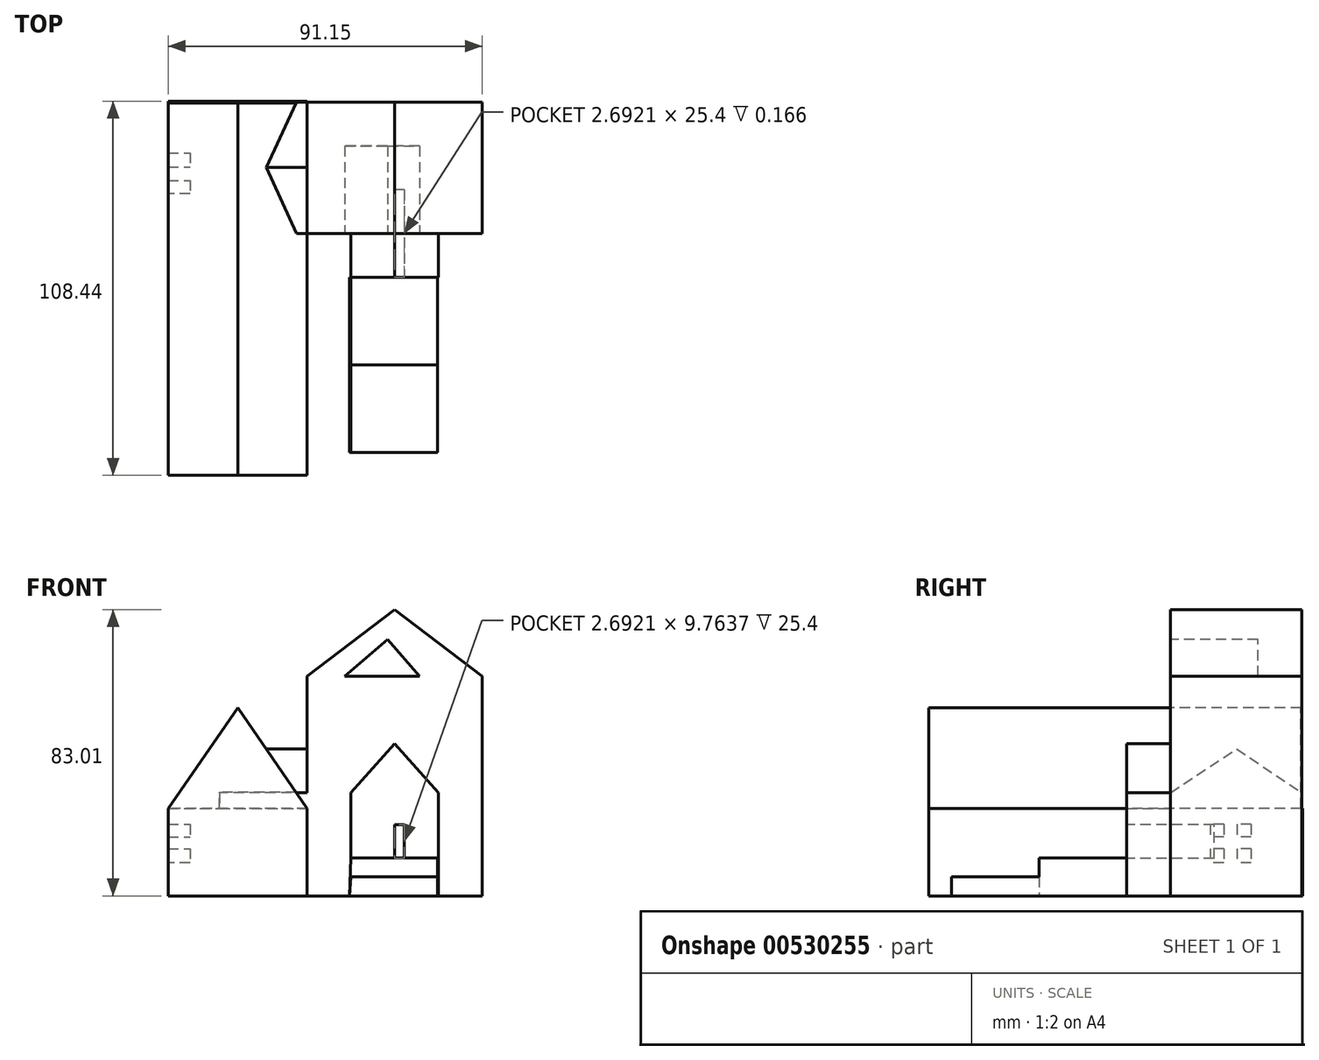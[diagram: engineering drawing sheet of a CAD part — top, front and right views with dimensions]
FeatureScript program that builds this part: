
annotation { "Feature Type Name" : "Feature", "Feature Type Description" : "" }
export const myFeature = defineFeature(function(context is Context, id is Id, definition is map)
    precondition{}
    {
        {
            var Q0;
            Q0=qCreatedBy(makeId("Right.planeOp"),FACE);
            var sketch = newSketch(context, id + "F0", { "sketchPlane" : qUnion([Q0])});
            skLineSegment(sketch, "E0.bottom", {"start": v(61.84, 29.91) * mm, "end": v(23.74, 29.91) * mm});
            skLineSegment(sketch, "E0.top", {"start": v(61.84, 10.86) * mm, "end": v(23.74, 10.86) * mm});
            skLineSegment(sketch, "E0.left", {"start": v(61.84, 29.91) * mm, "end": v(61.84, 10.86) * mm});
            skLineSegment(sketch, "E0.right", {"start": v(23.74, 29.91) * mm, "end": v(23.74, 10.86) * mm});
            skLineSegment(sketch, "E1", {"start": v(61.84, 29.91) * mm, "end": v(42.98, 42.61) * mm});
            skLineSegment(sketch, "E2", {"start": v(42.98, 42.61) * mm, "end": v(23.74, 29.91) * mm});
            skLineSegment(sketch, "E3", {"start": v(23.74, 29.91) * mm, "end": v(23.74, 42.61) * mm});
            skLineSegment(sketch, "E4", {"start": v(23.74, 42.61) * mm, "end": v(61.84, 42.61) * mm});
            skLineSegment(sketch, "E5", {"start": v(61.84, 42.61) * mm, "end": v(61.84, 29.91) * mm});
            skSolve(sketch);
        }
        {
            var Q0;
            Q0=makeQuery(id+"F0.imprint","IMPRINT",FACE,{"disambiguationData":[TD([[makeQuery(id+"F0.imprint","IMPRINT",EDGE,{"derivedFrom":sQuery(id+"F0.wireOp",EDGE,"E0.bottom")}),1.0]])]});
            var Q1;
            Q1=makeQuery(id+"F0.imprint","IMPRINT",FACE,{"disambiguationData":[TD([[makeQuery(id+"F0.imprint","IMPRINT",EDGE,{"derivedFrom":sQuery(id+"F0.wireOp",EDGE,"E0.bottom")}),-1.0]])]});
            extrude(context, id + "F1", {"entities" : qUnion([Q0, Q1]), "depth" : 50.8 * mm, "offsetDistance" : 25.4 * mm});
        }
        {
            var Q0;
            Q0=makeQuery(id+"F1.opExtrude","SWEPT_FACE",FACE,{"disambiguationData":[OSD([sQuery(id+"F0.wireOp",EDGE,"E0.right")])]});
            var sketch = newSketch(context, id + "F2", { "sketchPlane" : qUnion([Q0])});
            skLineSegment(sketch, "E6", {"start": v(12.7, 10.86) * mm, "end": v(12.7, 29.91) * mm});
            skLineSegment(sketch, "E7", {"start": v(12.7, 29.91) * mm, "end": v(38.1, 29.91) * mm});
            skLineSegment(sketch, "E8", {"start": v(38.1, 29.91) * mm, "end": v(38.1, 10.86) * mm});
            skLineSegment(sketch, "E9", {"start": v(38.1, 10.86) * mm, "end": v(12.7, 10.86) * mm});
            skSolve(sketch);
        }
        {
            var Q0;
            Q0 = qSketchRegion(id + "F2", true);
            extrude(context, id + "F3", {"entities" : qUnion([Q0]), "operationType" : NewBodyOperationType.ADD, "depth" : 12.7 * mm, "offsetDistance" : 25.4 * mm});
        }
        {
            var Q0;
            Q0=makeQuery(id+"F3.opExtrude","CAP_FACE",FACE,{"disambiguationData":[OSD([sQuery(id+"F2.wireOp",EDGE,"E6"),sQuery(id+"F2.wireOp",EDGE,"E7"),sQuery(id+"F2.wireOp",EDGE,"E8"),sQuery(id+"F2.wireOp",EDGE,"E9")])],"isStart":false});
            var sketch = newSketch(context, id + "F4", { "sketchPlane" : qUnion([Q0])});
            skLineSegment(sketch, "E10", {"start": v(12.7, 29.91) * mm, "end": v(25.4, 44.11) * mm});
            skLineSegment(sketch, "E11", {"start": v(25.4, 44.11) * mm, "end": v(38.1, 29.91) * mm});
            skLineSegment(sketch, "E12", {"start": v(38.1, 29.91) * mm, "end": v(12.7, 29.91) * mm});
            skSolve(sketch);
        }
        {
            var Q0;
            Q0 = qSketchRegion(id + "F4", true);
            extrude(context, id + "F5", {"entities" : qUnion([Q0]), "operationType" : NewBodyOperationType.ADD, "oppositeDirection" : true, "depth" : 31.75 * mm, "offsetDistance" : 25.4 * mm});
        }
        {
            var Q0;
            Q0=makeQuery(id+"F5.boolean.opBoolean","MERGE",FACE,{"derivedFrom":[makeQuery(id+"F3.opExtrude","CAP_FACE",FACE,{"disambiguationData":[OSD([sQuery(id+"F2.wireOp",EDGE,"E6"),sQuery(id+"F2.wireOp",EDGE,"E7"),sQuery(id+"F2.wireOp",EDGE,"E8"),sQuery(id+"F2.wireOp",EDGE,"E9")])],"isStart":false}),makeQuery(id+"F5.opExtrude","CAP_FACE",FACE,{"disambiguationData":[OSD([sQuery(id+"F4.wireOp",EDGE,"E10"),sQuery(id+"F4.wireOp",EDGE,"E11"),sQuery(id+"F4.wireOp",EDGE,"E12")])],"isStart":true})]});
            var sketch = newSketch(context, id + "F6", { "sketchPlane" : qUnion([Q0])});
            skLineSegment(sketch, "E13.bottom", {"start": v(25.4, 10.86) * mm, "end": v(28.1, 10.86) * mm});
            skLineSegment(sketch, "E13.top", {"start": v(25.4, 20.63) * mm, "end": v(28.1, 20.63) * mm});
            skLineSegment(sketch, "E13.left", {"start": v(25.4, 10.86) * mm, "end": v(25.4, 20.63) * mm});
            skLineSegment(sketch, "E13.right", {"start": v(28.1, 10.86) * mm, "end": v(28.1, 20.63) * mm});
            skSolve(sketch);
        }
        {
            var Q0;
            Q0=qCreatedBy(makeId("Top.planeOp"),FACE);
            var sketch = newSketch(context, id + "F7", { "sketchPlane" : qUnion([Q0])});
            skLineSegment(sketch, "E14", {"start": v(0, 62.13) * mm, "end": v(-40.35, 62.13) * mm});
            skLineSegment(sketch, "E15", {"start": v(-40.35, 62.13) * mm, "end": v(-40.35, -46.3) * mm});
            skLineSegment(sketch, "E16", {"start": v(-40.35, -46.3) * mm, "end": v(0, -46.3) * mm});
            skLineSegment(sketch, "E17", {"start": v(0, -46.3) * mm, "end": v(0, 23.84) * mm});
            skLineSegment(sketch, "E18", {"start": v(0, 23.84) * mm, "end": v(0, 62.13) * mm});
            skSolve(sketch);
        }
        {
            var Q0;
            Q0 = qSketchRegion(id + "F7", true);
            var Q1;
            Q1=makeQuery(id+"F7.imprint","IMPRINT",FACE,{"disambiguationData":[TD([[makeQuery(id+"F7.imprint","IMPRINT",EDGE,{"derivedFrom":sQuery(id+"F7.wireOp",EDGE,"E14")}),1.0]])]});
            extrude(context, id + "F8", {"entities" : qUnion([Q0, Q1]), "operationType" : NewBodyOperationType.ADD, "depth" : 25.4 * mm, "offsetDistance" : 25.4 * mm});
        }
        {
            var Q0;
            Q0=makeQuery(id+"F8.opExtrude","SWEPT_FACE",FACE,{"disambiguationData":[OSD([sQuery(id+"F7.wireOp",EDGE,"E16")])]});
            var sketch = newSketch(context, id + "F9", { "sketchPlane" : qUnion([Q0])});
            skLineSegment(sketch, "E19", {"start": v(-40.35, 25.4) * mm, "end": v(-20.17, 54.51) * mm});
            skPoint(sketch, "E19.endSnap0", {"position": v(-20.17, 25.4) * mm});
            skLineSegment(sketch, "E20", {"start": v(-20.17, 54.51) * mm, "end": v(0, 25.4) * mm});
            skLineSegment(sketch, "E21", {"start": v(0, 25.4) * mm, "end": v(-40.35, 25.4) * mm});
            skSolve(sketch);
        }
        {
            var Q0;
            Q0 = qSketchRegion(id + "F9", true);
            extrude(context, id + "F10", {"entities" : qUnion([Q0]), "operationType" : NewBodyOperationType.ADD, "oppositeDirection" : true, "depth" : 107.95 * mm, "offsetDistance" : 25.4 * mm});
        }
        {
            var Q0;
            Q0=makeQuery(id+"F1.opExtrude","CAP_FACE",FACE,{"disambiguationData":[OSD([sQuery(id+"F0.wireOp",EDGE,"E0.top"),sQuery(id+"F0.wireOp",EDGE,"E0.left"),sQuery(id+"F0.wireOp",EDGE,"E0.right"),sQuery(id+"F0.wireOp",EDGE,"E1"),sQuery(id+"F0.wireOp",EDGE,"E2")])],"isStart":false});
            var sketch = newSketch(context, id + "F11", { "sketchPlane" : qUnion([Q0])});
            skLineSegment(sketch, "E22", {"start": v(23.74, 10.86) * mm, "end": v(23.74, 0) * mm});
            skLineSegment(sketch, "E23", {"start": v(23.74, 0) * mm, "end": v(61.84, 0) * mm});
            skLineSegment(sketch, "E24", {"start": v(61.84, 0) * mm, "end": v(61.84, 10.86) * mm});
            skLineSegment(sketch, "E25", {"start": v(61.84, 10.86) * mm, "end": v(23.74, 10.86) * mm});
            skSolve(sketch);
        }
        {
            var Q0;
            Q0 = qSketchRegion(id + "F11", true);
            var Q1;
            Q1=makeQuery(id+"F11.imprint","IMPRINT",FACE,{"disambiguationData":[TD([[makeQuery(id+"F11.imprint","IMPRINT",EDGE,{"derivedFrom":sQuery(id+"F11.wireOp",EDGE,"E22")}),1.0]])]});
            extrude(context, id + "F12", {"entities" : qUnion([Q0, Q1]), "operationType" : NewBodyOperationType.ADD, "oppositeDirection" : true, "depth" : 50.8 * mm, "offsetDistance" : 25.4 * mm});
        }
        {
            var Q0;
            Q0=makeQuery(id+"F6.imprint","IMPRINT",FACE,{"disambiguationData":[TD([[makeQuery(id+"F6.imprint","IMPRINT",EDGE,{"derivedFrom":sQuery(id+"F6.wireOp",EDGE,"E13.top")}),1.0]])]});
            var sketch = newSketch(context, id + "F13", { "sketchPlane" : qUnion([Q0])});
            skLineSegment(sketch, "E26", {"start": v(12.69, 11.03) * mm, "end": v(37.75, 11.03) * mm});
            skLineSegment(sketch, "E27", {"start": v(37.75, 11.03) * mm, "end": v(37.75, 0) * mm});
            skLineSegment(sketch, "E28", {"start": v(37.75, 0) * mm, "end": v(12.22, 0) * mm});
            skLineSegment(sketch, "E29", {"start": v(12.22, 0) * mm, "end": v(12.69, 11.03) * mm});
            skSolve(sketch);
        }
        {
            var Q0;
            Q0 = qSketchRegion(id + "F13", true);
            extrude(context, id + "F14", {"entities" : qUnion([Q0]), "operationType" : NewBodyOperationType.ADD, "depth" : 25.4 * mm, "offsetDistance" : 25.4 * mm});
        }
        {
            var Q0;
            Q0=makeQuery(id+"F14.opExtrude","CAP_FACE",FACE,{"disambiguationData":[OSD([sQuery(id+"F13.wireOp",EDGE,"E26"),sQuery(id+"F13.wireOp",EDGE,"E27"),sQuery(id+"F13.wireOp",EDGE,"E28"),sQuery(id+"F13.wireOp",EDGE,"E29")])],"isStart":false});
            var sketch = newSketch(context, id + "F15", { "sketchPlane" : qUnion([Q0])});
            skLineSegment(sketch, "E30", {"start": v(37.75, 5.52) * mm, "end": v(12.69, 5.52) * mm});
            skLineSegment(sketch, "E31", {"start": v(12.69, 5.52) * mm, "end": v(12.22, 0) * mm});
            skLineSegment(sketch, "E32", {"start": v(12.22, 0) * mm, "end": v(37.75, 0) * mm});
            skLineSegment(sketch, "E33", {"start": v(37.75, 0) * mm, "end": v(37.75, 5.52) * mm});
            skSolve(sketch);
        }
        {
            var Q0;
            Q0 = qSketchRegion(id + "F15", true);
            extrude(context, id + "F16", {"entities" : qUnion([Q0]), "operationType" : NewBodyOperationType.ADD, "depth" : 25.4 * mm, "offsetDistance" : 25.4 * mm});
        }
        {
            var Q0;
            Q0=makeQuery(id+"F3.opExtrude","SWEPT_FACE",FACE,{"disambiguationData":[OSD([sQuery(id+"F2.wireOp",EDGE,"E8")])]});
            var sketch = newSketch(context, id + "F17", { "sketchPlane" : qUnion([Q0])});
            skLineSegment(sketch, "E34", {"start": v(11.04, 10.86) * mm, "end": v(23.74, 10.86) * mm});
            skLineSegment(sketch, "E35", {"start": v(23.74, 10.86) * mm, "end": v(23.74, 0) * mm});
            skLineSegment(sketch, "E36", {"start": v(23.74, 0) * mm, "end": v(11.04, 0) * mm});
            skLineSegment(sketch, "E37", {"start": v(11.04, 0) * mm, "end": v(11.04, 10.86) * mm});
            skSolve(sketch);
        }
        {
            var Q0;
            Q0=makeQuery(id+"F17.imprint","IMPRINT",FACE,{"disambiguationData":[TD([[makeQuery(id+"F17.imprint","IMPRINT",EDGE,{"derivedFrom":sQuery(id+"F17.wireOp",EDGE,"E34")}),-1.0]])]});
            extrude(context, id + "F18", {"entities" : qUnion([Q0]), "operationType" : NewBodyOperationType.ADD, "oppositeDirection" : true, "depth" : 25.4 * mm, "offsetDistance" : 25.4 * mm});
        }
        {
            var Q0;
            Q0=makeQuery(id+"F6.imprint","IMPRINT",FACE,{"disambiguationData":[TD([[makeQuery(id+"F6.imprint","IMPRINT",EDGE,{"derivedFrom":sQuery(id+"F6.wireOp",EDGE,"E13.bottom")}),-1.0]])]});
            extrude(context, id + "F19", {"entities" : qUnion([Q0]), "operationType" : NewBodyOperationType.REMOVE, "oppositeDirection" : true, "depth" : 25.4 * mm, "offsetDistance" : 25.4 * mm});
        }
        {
            var Q0;
            Q0=makeQuery(id+"F1.opExtrude","CAP_FACE",FACE,{"disambiguationData":[OSD([sQuery(id+"F0.wireOp",EDGE,"E0.top"),sQuery(id+"F0.wireOp",EDGE,"E0.left"),sQuery(id+"F0.wireOp",EDGE,"E0.right"),sQuery(id+"F0.wireOp",EDGE,"E1"),sQuery(id+"F0.wireOp",EDGE,"E2")])],"isStart":true});
            extrude(context, id + "F20", {"entities" : qUnion([Q0]), "operationType" : NewBodyOperationType.ADD, "depth" : 25.4 * mm, "offsetDistance" : 25.4 * mm});
        }
        {
            var Q0;
            Q0=makeQuery(id+"F8.opExtrude","SWEPT_FACE",FACE,{"disambiguationData":[OSD([sQuery(id+"F7.wireOp",EDGE,"E15")])]});
            var sketch = newSketch(context, id + "F21", { "sketchPlane" : qUnion([Q0])});
            skLineSegment(sketch, "E38.bottom", {"start": v(-47.17, 20.75) * mm, "end": v(-35.31, 20.75) * mm});
            skLineSegment(sketch, "E38.top", {"start": v(-47.17, 9.67) * mm, "end": v(-35.31, 9.67) * mm});
            skLineSegment(sketch, "E38.left", {"start": v(-47.17, 20.75) * mm, "end": v(-47.17, 9.67) * mm});
            skLineSegment(sketch, "E38.right", {"start": v(-35.31, 20.75) * mm, "end": v(-35.31, 9.67) * mm});
            skSolve(sketch);
        }
        {
            var Q0;
            Q0=makeQuery(id+"F21.imprint","IMPRINT",FACE,{"disambiguationData":[TD([[makeQuery(id+"F21.imprint","IMPRINT",EDGE,{"derivedFrom":sQuery(id+"F21.wireOp",EDGE,"E38.bottom")}),-1.0]])]});
            extrude(context, id + "F22", {"entities" : qUnion([Q0]), "operationType" : NewBodyOperationType.REMOVE, "oppositeDirection" : true, "depth" : 6.35 * mm, "offsetDistance" : 25.4 * mm});
        }
        {
            var Q0;
            Q0=makeQuery(id+"F22.boolean.opBoolean","COPY",FACE,{"derivedFrom":makeQuery(id+"F22.opExtrude","CAP_FACE",FACE,{"disambiguationData":[OSD([sQuery(id+"F21.wireOp",EDGE,"E38.bottom"),sQuery(id+"F21.wireOp",EDGE,"E38.top"),sQuery(id+"F21.wireOp",EDGE,"E38.left"),sQuery(id+"F21.wireOp",EDGE,"E38.right")])],"isStart":false})});
            var sketch = newSketch(context, id + "F23", { "sketchPlane" : qUnion([Q0])});
            skLineSegment(sketch, "E39.bottom", {"start": v(-47.17, 17.04) * mm, "end": v(-35.31, 17.04) * mm});
            skLineSegment(sketch, "E39.top", {"start": v(-47.17, 13.72) * mm, "end": v(-35.31, 13.72) * mm});
            skLineSegment(sketch, "E39.left", {"start": v(-47.17, 17.04) * mm, "end": v(-47.17, 13.72) * mm});
            skLineSegment(sketch, "E39.right", {"start": v(-35.31, 17.04) * mm, "end": v(-35.31, 13.72) * mm});
            skLineSegment(sketch, "E40.bottom", {"start": v(-43.08, 20.75) * mm, "end": v(-39.2, 20.75) * mm});
            skLineSegment(sketch, "E40.top", {"start": v(-43.08, 9.67) * mm, "end": v(-39.2, 9.67) * mm});
            skLineSegment(sketch, "E40.left", {"start": v(-43.08, 20.75) * mm, "end": v(-43.08, 9.67) * mm});
            skLineSegment(sketch, "E40.right", {"start": v(-39.2, 20.75) * mm, "end": v(-39.2, 9.67) * mm});
            skSolve(sketch);
        }
        {
            var Q0;
            {var subQ0=sQuery(id+"F23.wireOp",EDGE,"E39.left");Q0=makeQuery(id+"F23.imprint","IMPRINT",FACE,{"disambiguationData":[TD([[makeQuery(id+"F23.imprint","IMPRINT",EDGE,{"derivedFrom":subQ0}),1.0]])]});}
            var Q1;
            {var subQ0=sQuery(id+"F23.wireOp",EDGE,"E40.left");var subQ1=sQuery(id+"F23.wireOp",EDGE,"E39.bottom");var subQ2=makeQuery(id+"F23.imprint","INTERSECT",VERTEX,{"derivedFrom":[subQ1,subQ0]});Q1=makeQuery(id+"F23.imprint","IMPRINT",FACE,{"disambiguationData":[TD([[makeQuery(id+"F23.imprint","IMPRINT",EDGE,{"disambiguationData":[TD([[subQ2,-1.0]])],"derivedFrom":subQ1}),-1.0]])]});}
            var Q2;
            {var subQ5=sQuery(id+"F23.wireOp",EDGE,"E40.bottom");Q2=makeQuery(id+"F23.imprint","IMPRINT",FACE,{"disambiguationData":[TD([[makeQuery(id+"F23.imprint","IMPRINT",EDGE,{"derivedFrom":subQ5}),-1.0]])]});}
            var Q3;
            {var subQ0=sQuery(id+"F23.wireOp",EDGE,"E39.right");Q3=makeQuery(id+"F23.imprint","IMPRINT",FACE,{"disambiguationData":[TD([[makeQuery(id+"F23.imprint","IMPRINT",EDGE,{"derivedFrom":subQ0}),-1.0]])]});}
            var Q4;
            {var subQ5=sQuery(id+"F23.wireOp",EDGE,"E40.top");Q4=makeQuery(id+"F23.imprint","IMPRINT",FACE,{"disambiguationData":[TD([[makeQuery(id+"F23.imprint","IMPRINT",EDGE,{"derivedFrom":subQ5}),1.0]])]});}
            extrude(context, id + "F24", {"entities" : qUnion([Q0, Q1, Q2, Q3, Q4]), "operationType" : NewBodyOperationType.ADD, "depth" : 6.35 * mm, "offsetDistance" : 25.4 * mm});
        }
        {
            var Q0;
            {var subQ1=sQuery(id+"F11.wireOp",EDGE,"E22");var subQ5=sQuery(id+"F0.wireOp",EDGE,"E0.right");var subQ9=makeQuery(id+"F3.opExtrude","SWEPT_FACE",FACE,{"disambiguationData":[OSD([sQuery(id+"F2.wireOp",EDGE,"E8")])]});var subQ14=makeQuery(id+"F1.opExtrude","SWEPT_FACE",FACE,{"disambiguationData":[OSD([subQ5])]});Q0=makeQuery(id+"F18.boolean.opBoolean","SPLIT",FACE,{"disambiguationData":[TD([subQ9])],"derivedFrom":makeQuery(id+"F12.boolean.opBoolean","MERGE",FACE,{"derivedFrom":[makeQuery(id+"F3.boolean.opBoolean","SPLIT",FACE,{"disambiguationData":[TD([makeQuery(id+"F3.opExtrude","SWEPT_FACE",FACE,{"disambiguationData":[OSD([sQuery(id+"F2.wireOp",EDGE,"E6")])]})])],"derivedFrom":subQ14}),makeQuery(id+"F3.boolean.opBoolean","SPLIT",FACE,{"disambiguationData":[TD([subQ9])],"derivedFrom":subQ14}),makeQuery(id+"F12.opExtrude","SWEPT_FACE",FACE,{"disambiguationData":[OSD([subQ1])]})]})});}
            var sketch = newSketch(context, id + "F25", { "sketchPlane" : qUnion([Q0])});
            skLineSegment(sketch, "E41", {"start": v(50.8, 29.91) * mm, "end": v(50.8, 63.72) * mm});
            skLineSegment(sketch, "E42", {"start": v(50.8, 63.72) * mm, "end": v(0, 63.72) * mm});
            skLineSegment(sketch, "E43", {"start": v(0, 63.72) * mm, "end": v(0, 29.91) * mm});
            skLineSegment(sketch, "E44", {"start": v(0, 29.91) * mm, "end": v(50.8, 29.91) * mm});
            skSolve(sketch);
        }
        {
            var Q0;
            {var subQ3=sQuery(id+"F25.wireOp",EDGE,"E41");Q0=makeQuery(id+"F25.imprint","IMPRINT",FACE,{"disambiguationData":[TD([[makeQuery(id+"F25.imprint","IMPRINT",EDGE,{"derivedFrom":subQ3}),1.0]])]});}
            extrude(context, id + "F26", {"entities" : qUnion([Q0]), "operationType" : NewBodyOperationType.ADD, "oppositeDirection" : true, "depth" : 38.1 * mm, "offsetDistance" : 25.4 * mm});
        }
        {
            var Q0;
            {var subQ0=sQuery(id+"F0.wireOp",EDGE,"E0.right");var subQ6=makeQuery(id+"F3.opExtrude","SWEPT_FACE",FACE,{"disambiguationData":[OSD([sQuery(id+"F2.wireOp",EDGE,"E6")])]});var subQ20=sQuery(id+"F11.wireOp",EDGE,"E22");var subQ25=makeQuery(id+"F3.opExtrude","SWEPT_FACE",FACE,{"disambiguationData":[OSD([sQuery(id+"F2.wireOp",EDGE,"E8")])]});var subQ26=makeQuery(id+"F1.opExtrude","SWEPT_FACE",FACE,{"disambiguationData":[OSD([subQ0])]});var subQ27=makeQuery(id+"F12.boolean.opBoolean","MERGE",FACE,{"derivedFrom":[makeQuery(id+"F3.boolean.opBoolean","SPLIT",FACE,{"disambiguationData":[TD([subQ6])],"derivedFrom":subQ26}),makeQuery(id+"F3.boolean.opBoolean","SPLIT",FACE,{"disambiguationData":[TD([subQ25])],"derivedFrom":subQ26}),makeQuery(id+"F12.opExtrude","SWEPT_FACE",FACE,{"disambiguationData":[OSD([subQ20])]})]});Q0=makeQuery(id+"F26.boolean.opBoolean","MERGE",FACE,{"derivedFrom":[makeQuery(id+"F18.boolean.opBoolean","SPLIT",FACE,{"disambiguationData":[TD([subQ25])],"derivedFrom":subQ27}),makeQuery(id+"F20.boolean.opBoolean","MERGE",FACE,{"derivedFrom":[makeQuery(id+"F18.boolean.opBoolean","SPLIT",FACE,{"disambiguationData":[TD([subQ6])],"derivedFrom":subQ27}),makeQuery(id+"F20.opExtrude","SWEPT_FACE",FACE,{"disambiguationData":[OSD([subQ0])]})]}),makeQuery(id+"F26.opExtrude","CAP_FACE",FACE,{"disambiguationData":[OSD([sQuery(id+"F25.wireOp",EDGE,"E41"),sQuery(id+"F25.wireOp",EDGE,"E42"),sQuery(id+"F25.wireOp",EDGE,"E43"),sQuery(id+"F25.wireOp",EDGE,"E44")])],"isStart":true})]});}
            var sketch = newSketch(context, id + "F27", { "sketchPlane" : qUnion([Q0])});
            skLineSegment(sketch, "E45", {"start": v(0, 63.72) * mm, "end": v(25.4, 83) * mm});
            skPoint(sketch, "E45.endSnap0", {"position": v(25.4, 63.72) * mm});
            skLineSegment(sketch, "E46", {"start": v(25.4, 83) * mm, "end": v(50.8, 63.72) * mm});
            skLineSegment(sketch, "E47", {"start": v(50.8, 63.72) * mm, "end": v(0, 63.72) * mm});
            skSolve(sketch);
        }
        {
            var Q0;
            Q0=makeQuery(id+"F27.imprint","IMPRINT",FACE,{"disambiguationData":[TD([[makeQuery(id+"F27.imprint","IMPRINT",EDGE,{"derivedFrom":sQuery(id+"F27.wireOp",EDGE,"E45")}),-1.0]])]});
            extrude(context, id + "F28", {"entities" : qUnion([Q0]), "operationType" : NewBodyOperationType.ADD, "oppositeDirection" : true, "depth" : 38.1 * mm, "offsetDistance" : 25.4 * mm});
        }
        {
            var Q0;
            {var subQ0=sQuery(id+"F0.wireOp",EDGE,"E0.right");var subQ6=makeQuery(id+"F3.opExtrude","SWEPT_FACE",FACE,{"disambiguationData":[OSD([sQuery(id+"F2.wireOp",EDGE,"E6")])]});var subQ20=sQuery(id+"F11.wireOp",EDGE,"E22");var subQ25=makeQuery(id+"F3.opExtrude","SWEPT_FACE",FACE,{"disambiguationData":[OSD([sQuery(id+"F2.wireOp",EDGE,"E8")])]});var subQ26=makeQuery(id+"F1.opExtrude","SWEPT_FACE",FACE,{"disambiguationData":[OSD([subQ0])]});var subQ27=makeQuery(id+"F12.boolean.opBoolean","MERGE",FACE,{"derivedFrom":[makeQuery(id+"F3.boolean.opBoolean","SPLIT",FACE,{"disambiguationData":[TD([subQ6])],"derivedFrom":subQ26}),makeQuery(id+"F3.boolean.opBoolean","SPLIT",FACE,{"disambiguationData":[TD([subQ25])],"derivedFrom":subQ26}),makeQuery(id+"F12.opExtrude","SWEPT_FACE",FACE,{"disambiguationData":[OSD([subQ20])]})]});Q0=makeQuery(id+"F28.boolean.opBoolean","MERGE",FACE,{"derivedFrom":[makeQuery(id+"F26.boolean.opBoolean","MERGE",FACE,{"derivedFrom":[makeQuery(id+"F18.boolean.opBoolean","SPLIT",FACE,{"disambiguationData":[TD([subQ25])],"derivedFrom":subQ27}),makeQuery(id+"F20.boolean.opBoolean","MERGE",FACE,{"derivedFrom":[makeQuery(id+"F18.boolean.opBoolean","SPLIT",FACE,{"disambiguationData":[TD([subQ6])],"derivedFrom":subQ27}),makeQuery(id+"F20.opExtrude","SWEPT_FACE",FACE,{"disambiguationData":[OSD([subQ0])]})]}),makeQuery(id+"F26.opExtrude","CAP_FACE",FACE,{"disambiguationData":[OSD([sQuery(id+"F25.wireOp",EDGE,"E41"),sQuery(id+"F25.wireOp",EDGE,"E42"),sQuery(id+"F25.wireOp",EDGE,"E43"),sQuery(id+"F25.wireOp",EDGE,"E44")])],"isStart":true})]}),makeQuery(id+"F28.opExtrude","CAP_FACE",FACE,{"disambiguationData":[OSD([sQuery(id+"F27.wireOp",EDGE,"E45"),sQuery(id+"F27.wireOp",EDGE,"E46"),sQuery(id+"F27.wireOp",EDGE,"E47")])],"isStart":true})]});}
            var sketch = newSketch(context, id + "F29", { "sketchPlane" : qUnion([Q0])});
            skLineSegment(sketch, "E48", {"start": v(10.87, 63.72) * mm, "end": v(23.34, 74.41) * mm});
            skLineSegment(sketch, "E49", {"start": v(23.34, 74.41) * mm, "end": v(32.52, 63.72) * mm});
            skLineSegment(sketch, "E50", {"start": v(32.52, 63.72) * mm, "end": v(10.87, 63.72) * mm});
            skSolve(sketch);
        }
        {
            var Q0;
            Q0 = qSketchRegion(id + "F29", true);
            extrude(context, id + "F30", {"entities" : qUnion([Q0]), "operationType" : NewBodyOperationType.REMOVE, "oppositeDirection" : true, "depth" : 25.4 * mm, "offsetDistance" : 25.4 * mm});
        }
    });
